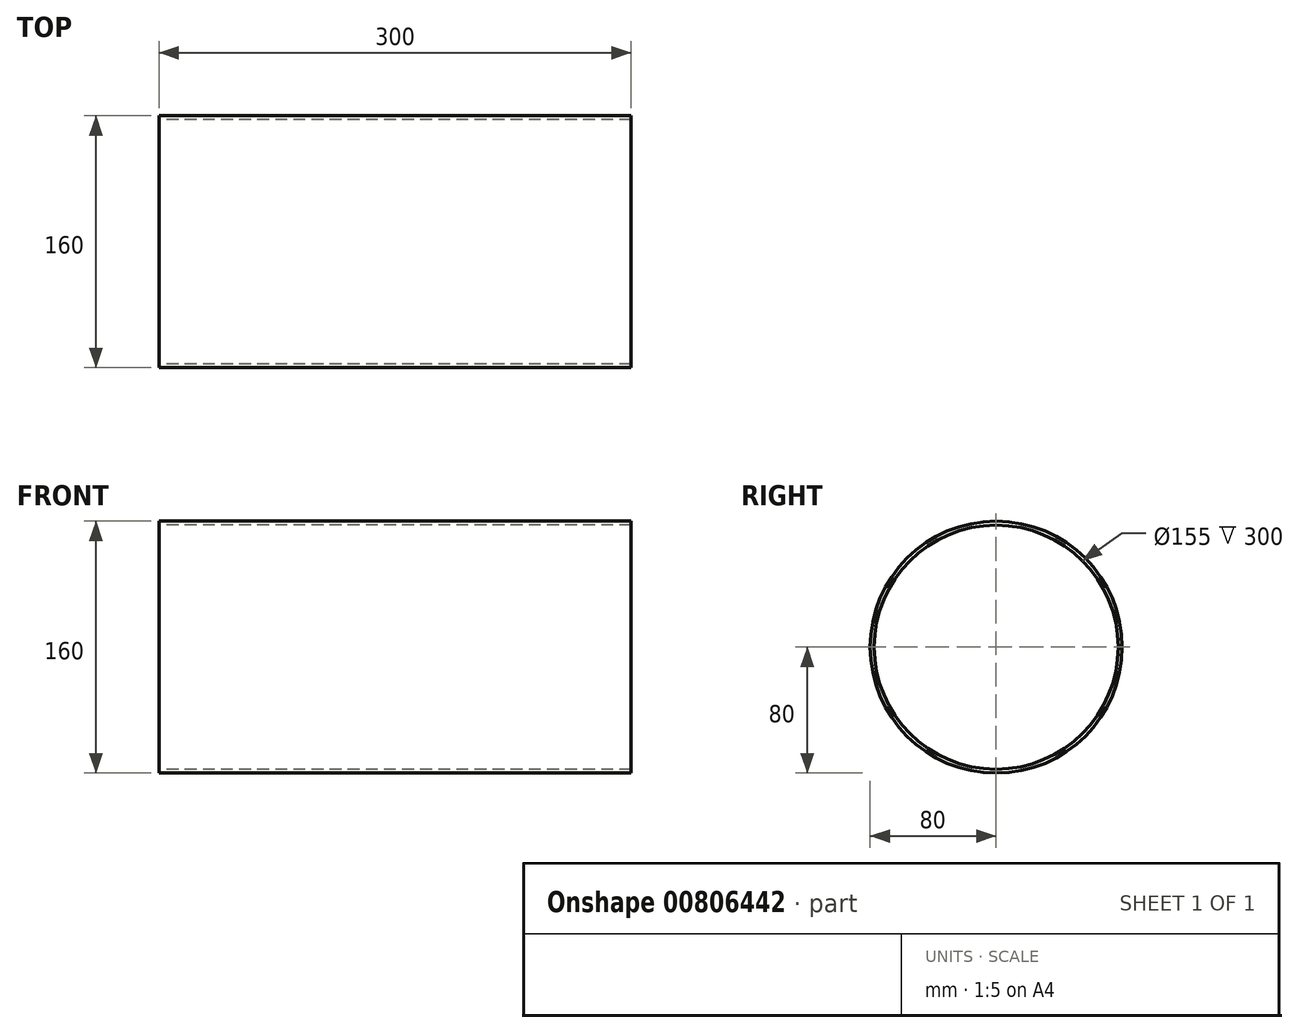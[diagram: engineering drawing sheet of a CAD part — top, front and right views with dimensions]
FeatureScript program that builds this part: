
annotation { "Feature Type Name" : "Feature", "Feature Type Description" : "" }
export const myFeature = defineFeature(function(context is Context, id is Id, definition is map)
    precondition{}
    {
        {
            var Q0;
            Q0=qCreatedBy(makeId("Right.planeOp"),FACE);
            var sketch = newSketch(context, id + "F0", { "sketchPlane" : qUnion([Q0])});
            skCircle(sketch, "E0", {"center": v(0, 0) * mm, "radius": 77.5 * mm});
            skCircle(sketch, "E1", {"center": v(0, 0) * mm, "radius": 80 * mm});
            skSolve(sketch);
        }
        {
            var Q0;
            Q0=makeQuery(id+"F0.imprint","IMPRINT",FACE,{"disambiguationData":[TD([[makeQuery(id+"F0.imprint","IMPRINT",EDGE,{"derivedFrom":sQuery(id+"F0.wireOp",EDGE,"E0")}),-1.0]])]});
            extrude(context, id + "F1", {"entities" : qUnion([Q0]), "depth" : 300 * mm, "offsetDistance" : 25 * mm});
        }
    });
